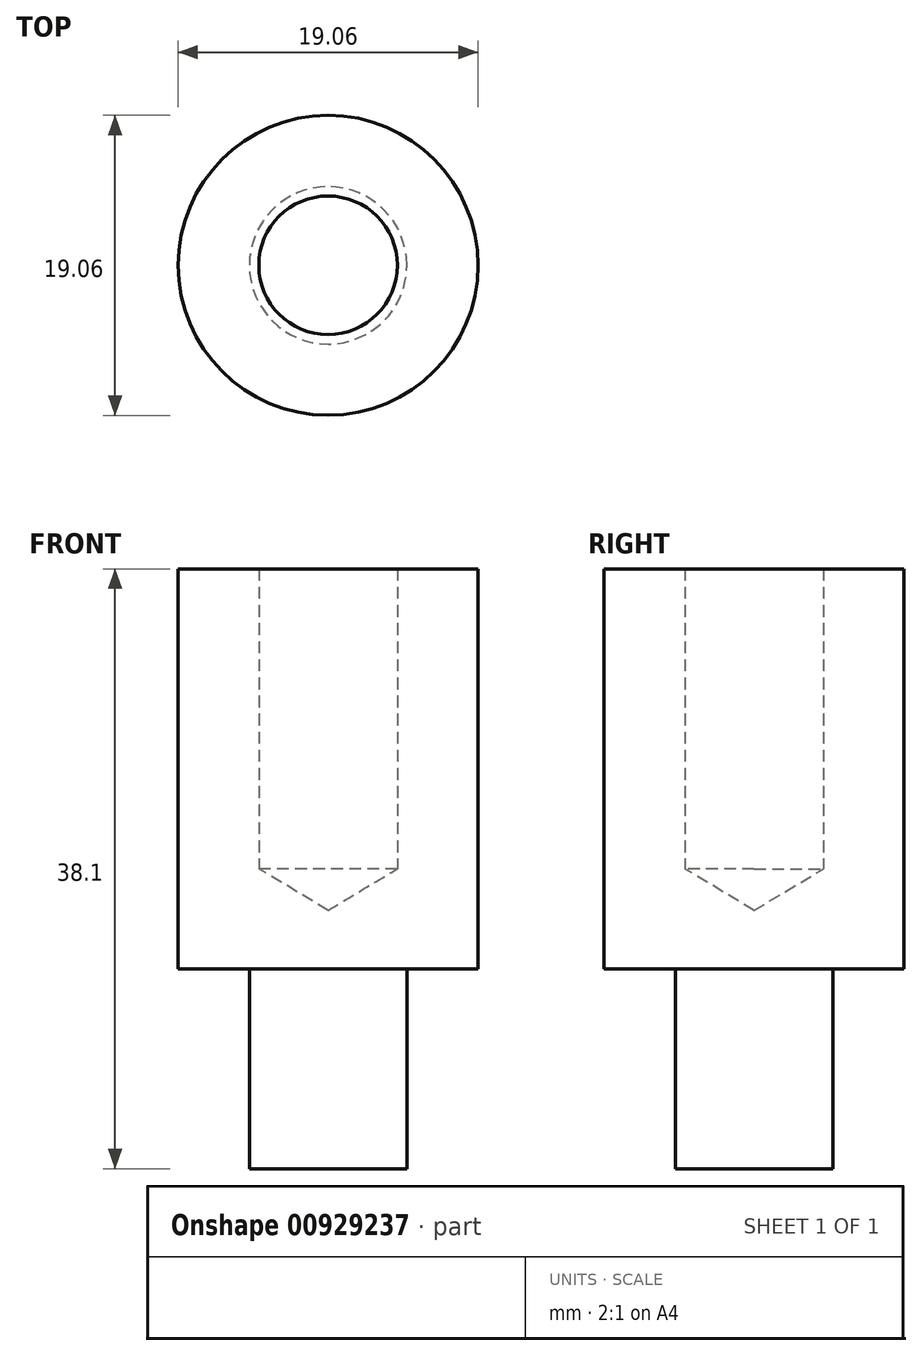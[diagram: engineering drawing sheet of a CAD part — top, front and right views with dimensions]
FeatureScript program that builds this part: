
annotation { "Feature Type Name" : "Feature", "Feature Type Description" : "" }
export const myFeature = defineFeature(function(context is Context, id is Id, definition is map)
    precondition{}
    {
        {
            var Q0;
            Q0=qCreatedBy(makeId("Top.planeOp"),FACE);
            var sketch = newSketch(context, id + "F0", { "sketchPlane" : qUnion([Q0])});
            skCircle(sketch, "E0", {"center": v(0, 0) * mm, "radius": 9.53 * mm});
            skCircle(sketch, "E1", {"center": v(0, 0) * mm, "radius": 5 * mm});
            skSolve(sketch);
        }
        {
            var Q0;
            Q0=makeQuery(id+"F0.imprint","IMPRINT",FACE,{"disambiguationData":[TD([[makeQuery(id+"F0.imprint","IMPRINT",EDGE,{"derivedFrom":sQuery(id+"F0.wireOp",EDGE,"E0")}),1.0]])]});
            var Q1;
            Q1=makeQuery(id+"F0.imprint","IMPRINT",FACE,{"disambiguationData":[TD([[makeQuery(id+"F0.imprint","IMPRINT",EDGE,{"derivedFrom":sQuery(id+"F0.wireOp",EDGE,"E1")}),1.0]])]});
            extrude(context, id + "F1", {"entities" : qUnion([Q0, Q1]), "depth" : 25.4 * mm, "offsetDistance" : 25.4 * mm});
        }
        {
            var Q0;
            Q0=makeQuery(id+"F0.imprint","IMPRINT",FACE,{"disambiguationData":[TD([[makeQuery(id+"F0.imprint","IMPRINT",EDGE,{"derivedFrom":sQuery(id+"F0.wireOp",EDGE,"E1")}),1.0]])]});
            extrude(context, id + "F2", {"entities" : qUnion([Q0]), "operationType" : NewBodyOperationType.ADD, "oppositeDirection" : true, "depth" : 12.7 * mm, "offsetDistance" : 25.4 * mm});
        }
        {
            var Q0;
            Q0=makeQuery(id+"F1.opExtrude","CAP_FACE",FACE,{"disambiguationData":[OSD([sQuery(id+"F0.wireOp",EDGE,"E0")])],"isStart":false});
            var sketch = newSketch(context, id + "F3", { "sketchPlane" : qUnion([Q0])});
            skPoint(sketch, "E2", {"position": v(0, 0) * mm});
            skSolve(sketch);
        }
        {
            var Q0;
            Q0=sQuery(id+"F3.wireOp",VERTEX,"E2");
            var Q1;
            Q1=makeQuery(id+"F1.opExtrude","SWEPT_BODY",BODY,{"disambiguationData":[OSD([sQuery(id+"F0.wireOp",EDGE,"E0")])]});
            hole(context, id + "F4", {"style" : HoleStyle.SIMPLE, "endStyle" : HoleEndStyle.BLIND, "standardTappedOrClearance" : lookupTablePath({ "standard" : "ISO", "engagement" : "75%", "pitch" : "1.25 mm", "size" : "M10", "type" : "Tapped" }), "standardBlindInLast" : lookupTablePath({ "standard" : "ISO", "fit" : "Normal", "engagement" : "75%", "pitch" : "1.25 mm", "size" : "M10", "type" : "Clearance & tapped" }), "holeDiameter" : 8.8 * mm, "majorDiameter" : 10 * mm, "showTappedDepth" : true, "holeDepth" : 19.05 * mm, "isTappedThrough" : true, "tappedDepth" : 15.3 * mm, "tapClearance" : 3, "locations" : qUnion([Q0]), "scope" : qUnion([Q1])});
        }
    });
